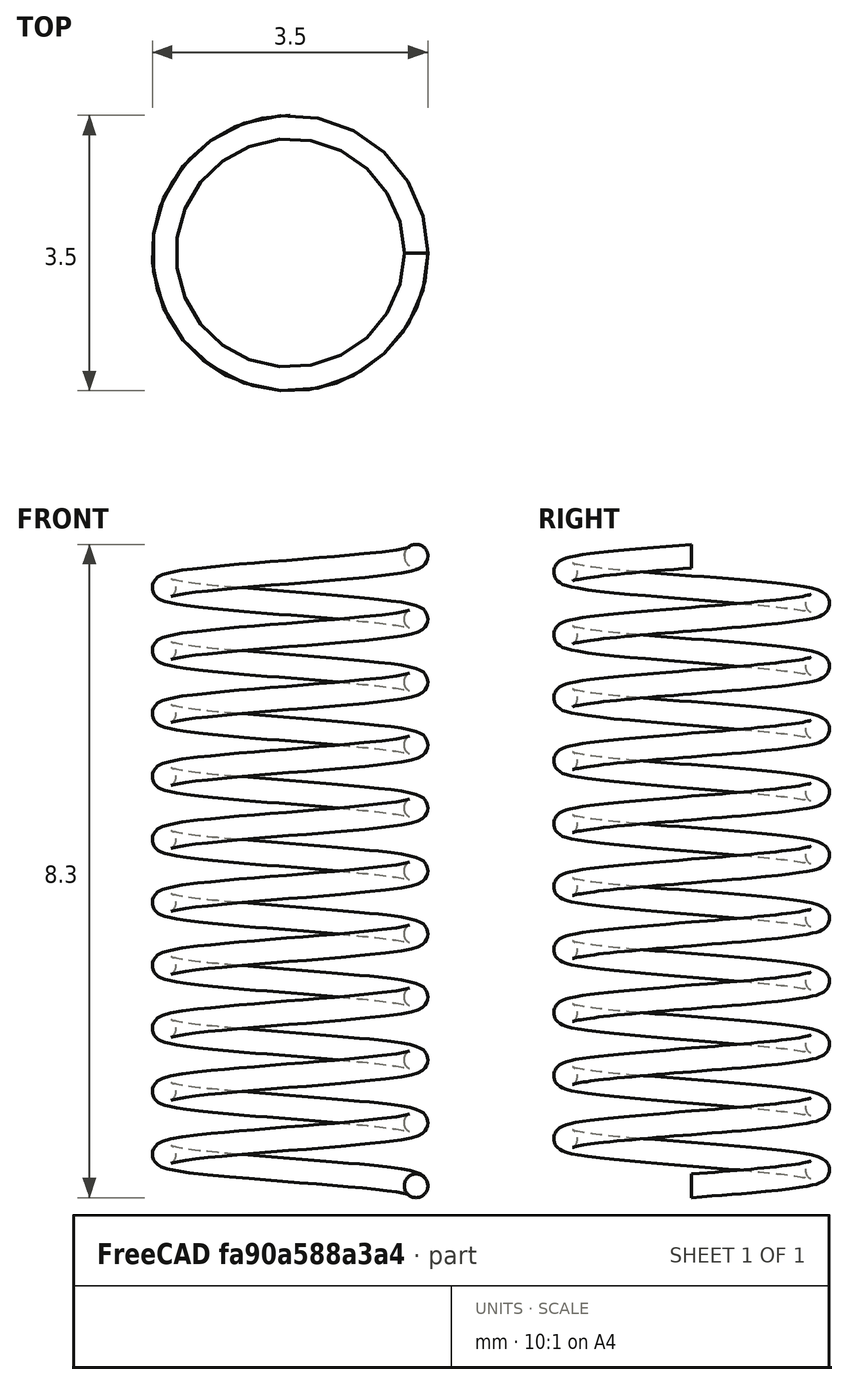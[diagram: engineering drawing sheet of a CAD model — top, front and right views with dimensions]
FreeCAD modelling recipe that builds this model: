
FCSTD DOCUMENT  (FreeCAD 0.20R29177 +233 (Git))
Label: spring_valve01
License: All rights reserved
LicenseURL: http://en.wikipedia.org/wiki/All_rights_reserved
objects: Spreadsheet::Sheet×1, Sketcher::SketchObject×1, PartDesign::AdditiveHelix×1, PartDesign::Body×1
note: 4 computed .brp shape members not serialized (recipe doc carries the construction recipe); baked Part::Feature solids carry a one-line shape summary decoded from their .brp

FEATURE [Spreadsheet::Sheet] Spreadsheet
  cells = B3=spring; C3=wire; D3=coil; E3=delta; F3=h_spring; G3=n_coil; H3=press ; C4(wire)=0.3; D4(coil)=1.6; E4(dt)=5; F4(hs)=8; G4(nc)=10; H4(prs)=3
FEATURE [Sketcher::SketchObject] Sketch
  FullyConstrained = true
  MapMode = 5
  Placement = pos=(0,0,0) rot=(1,0,0;1.5708rad)
  Support = -> [XZ_Plane]
  expr: Constraints[1] = Spreadsheet.wire
  expr: Constraints[2] = Spreadsheet.coil
  sketch-geometry (1):
    g0: Circle CenterX=1.6 CenterY=0 CenterZ=0 NormalX=0 NormalY=0 NormalZ=1 AngleXU=0 Radius=0.15
  constraints (3):
    c: PointOnObject(g0,g-1)
    c: Diameter(g0) = 0.3
    c: Distance(g-1,g0) = 1.6
FEATURE [PartDesign::AdditiveHelix] AdditiveHelix
  Angle = 0
  Axis = (0,-2e-16,1)
  Base = (0,0,0)
  Growth = 0
  HasBeenEdited = true
  Height = 8
  LeftHanded = false
  Mode = 2
  Outside = false
  Pitch = 0.8
  Placement = pos=(0,0,0) rot=(1,0,0;1.5708rad)
  Profile = -> Sketch
  ReferenceAxis = -> Sketch [V_Axis]
  Turns = 10
  expr: Height = Spreadsheet.hs
  expr: Turns = Spreadsheet.nc
FEATURE [PartDesign::Body] Body
  Group = -> [Sketch,AdditiveHelix]
  Origin = -> Origin
  Tip = -> AdditiveHelix
